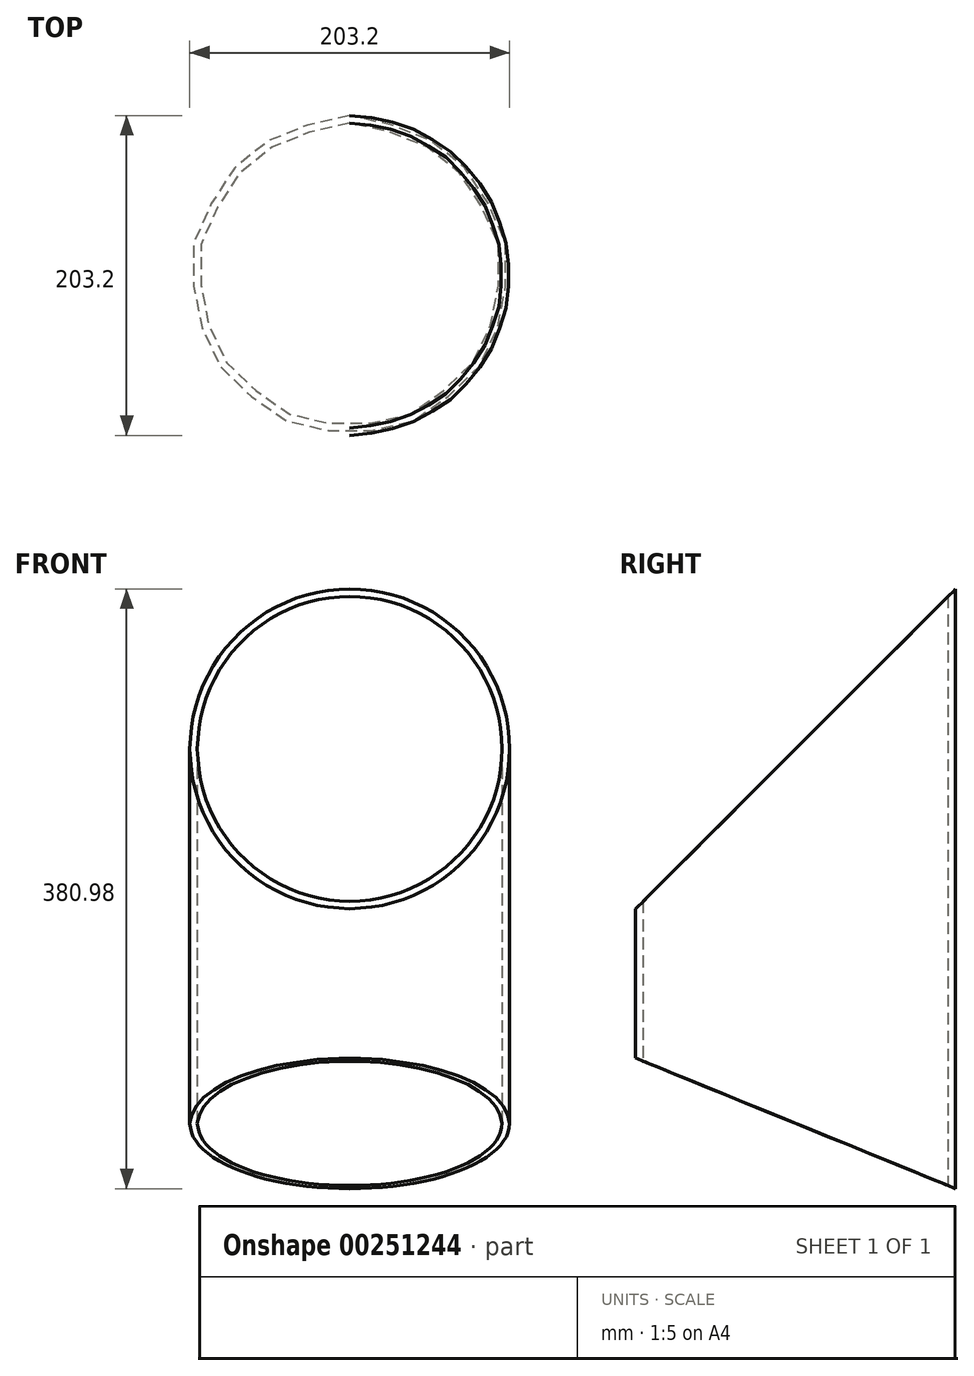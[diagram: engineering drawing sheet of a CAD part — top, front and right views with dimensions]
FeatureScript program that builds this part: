
annotation { "Feature Type Name" : "Feature", "Feature Type Description" : "" }
export const myFeature = defineFeature(function(context is Context, id is Id, definition is map)
    precondition{}
    {
        {
            var Q0;
            Q0=qCreatedBy(makeId("Top.planeOp"),FACE);
            var sketch = newSketch(context, id + "F0", { "sketchPlane" : qUnion([Q0])});
            skCircle(sketch, "E0", {"center": v(0, 0) * mm, "radius": 101.6 * mm});
            skCircle(sketch, "E1", {"center": v(0, 0) * mm, "radius": 96.84 * mm});
            skSolve(sketch);
        }
        {
            var Q0;
            Q0 = qSketchRegion(id + "F0", true);
            extrude(context, id + "F1", {"entities" : qUnion([Q0]), "depth" : 381 * mm});
        }
        {
            var Q0;
            Q0=qCreatedBy(makeId("Right.planeOp"),FACE);
            var sketch = newSketch(context, id + "F2", { "sketchPlane" : qUnion([Q0])});
            skLineSegment(sketch, "E2", {"start": v(101.6, 381) * mm, "end": v(-127, 381) * mm});
            skLineSegment(sketch, "E3", {"start": v(-127, 381) * mm, "end": v(-127, 152.4) * mm});
            skLineSegment(sketch, "E4", {"start": v(-126.94, 93.29) * mm, "end": v(-126.94, 0) * mm});
            skLineSegment(sketch, "E5", {"start": v(-126.94, 0) * mm, "end": v(101.66, 0) * mm});
            skLineSegment(sketch, "E6", {"start": v(101.6, 381) * mm, "end": v(-127, 152.4) * mm});
            skPoint(sketch, "E7.end.orphan", {"position": v(110.15, 381) * mm});
            skLineSegment(sketch, "E8", {"start": v(101.66, 0) * mm, "end": v(-126.94, 93.29) * mm});
            skSolve(sketch);
        }
        {
            var Q0;
            Q0 = qSketchRegion(id + "F2", true);
            extrude(context, id + "F3", {"entities" : qUnion([Q0]), "operationType" : NewBodyOperationType.REMOVE, "endBound" : BoundingType.THROUGH_ALL, "oppositeDirection" : true, "depth" : 25.4 * mm, "hasSecondDirection" : true, "secondDirectionBound" : SecondDirectionBoundingType.THROUGH_ALL, "secondDirectionOppositeDirection" : false, "secondDirectionDepth" : 25.4 * mm});
        }
    });
